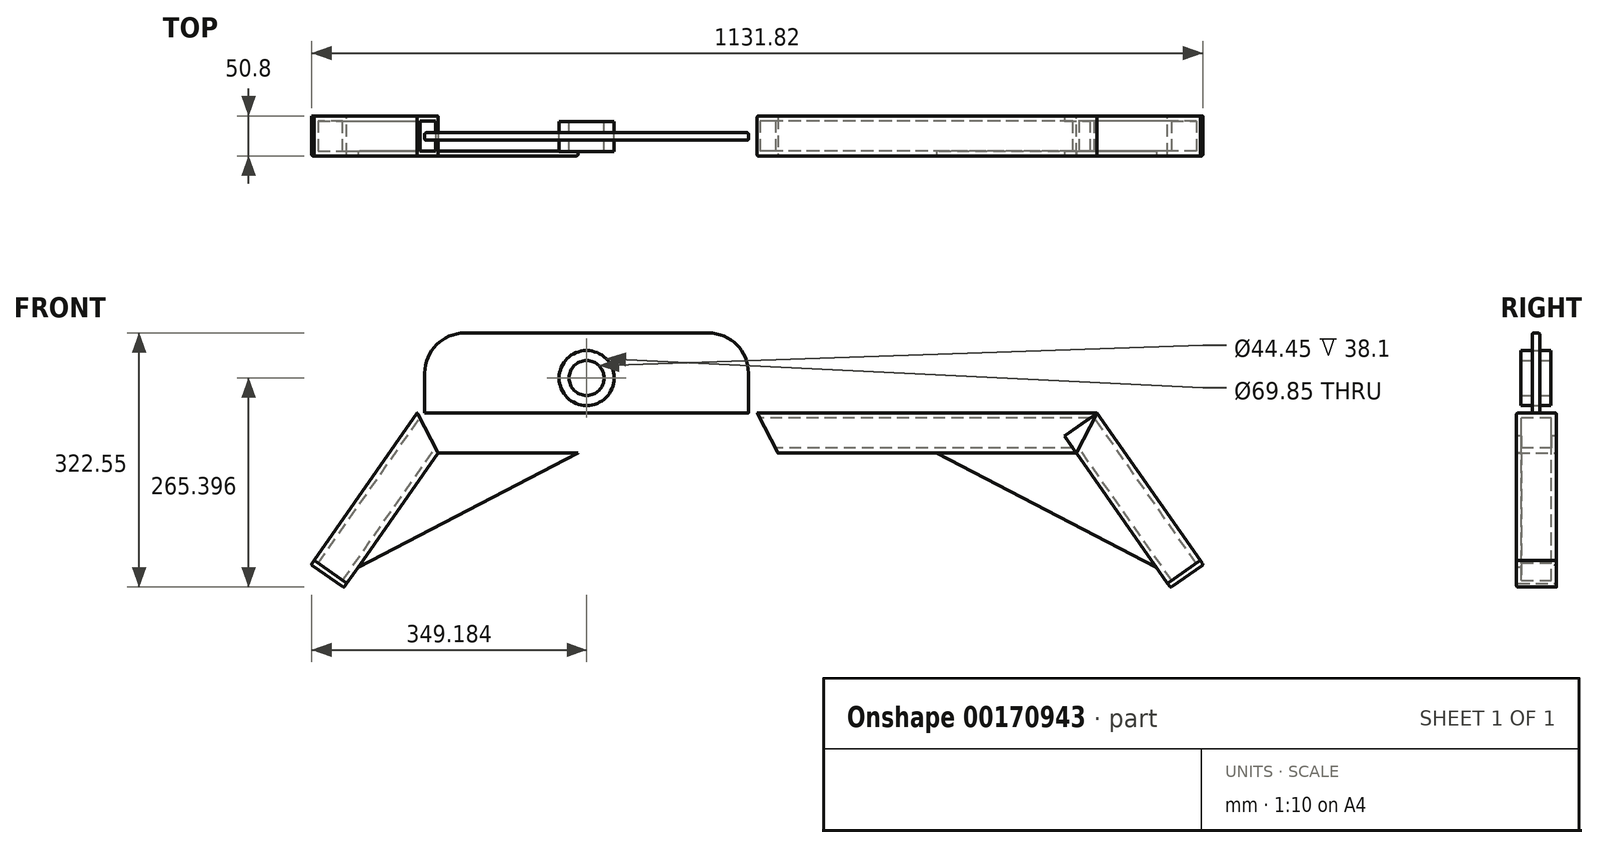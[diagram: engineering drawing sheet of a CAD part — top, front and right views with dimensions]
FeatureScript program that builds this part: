
annotation { "Feature Type Name" : "Feature", "Feature Type Description" : "" }
export const myFeature = defineFeature(function(context is Context, id is Id, definition is map)
    precondition{}
    {
        {
            var Q0;
            Q0=qCreatedBy(makeId("Right.planeOp"),FACE);
            var sketch = newSketch(context, id + "F0", { "sketchPlane" : qUnion([Q0])});
            skLineSegment(sketch, "E0.bottom", {"start": v(-57.95, 45.94) * mm, "end": v(-7.15, 45.94) * mm});
            skLineSegment(sketch, "E0.top", {"start": v(-57.95, -4.86) * mm, "end": v(-7.15, -4.86) * mm});
            skLineSegment(sketch, "E0.left", {"start": v(-57.95, 45.94) * mm, "end": v(-57.95, -4.86) * mm});
            skLineSegment(sketch, "E0.right", {"start": v(-7.15, 45.94) * mm, "end": v(-7.15, -4.86) * mm});
            skLineSegment(sketch, "E1.0", {"start": v(-13.5, 39.59) * mm, "end": v(-13.5, 1.49) * mm});
            skLineSegment(sketch, "E1.1", {"start": v(-51.6, 39.59) * mm, "end": v(-13.5, 39.59) * mm});
            skLineSegment(sketch, "E1.2", {"start": v(-51.6, 39.59) * mm, "end": v(-51.6, 1.49) * mm});
            skLineSegment(sketch, "E1.3", {"start": v(-51.6, 1.49) * mm, "end": v(-13.5, 1.49) * mm});
            skSolve(sketch);
        }
        {
            var Q0;
            Q0=makeQuery(id+"F0.imprint","IMPRINT",FACE,{"disambiguationData":[TD([[makeQuery(id+"F0.imprint","IMPRINT",EDGE,{"derivedFrom":sQuery(id+"F0.wireOp",EDGE,"E0.bottom")}),-1.0]])]});
            extrude(context, id + "F1", {"entities" : qUnion([Q0]), "depth" : 431.8 * mm});
        }
        {
            var Q0;
            Q0=makeQuery(id+"F1.opExtrude","SWEPT_FACE",FACE,{"disambiguationData":[OSD([sQuery(id+"F0.wireOp",EDGE,"E0.right")])]});
            var sketch = newSketch(context, id + "F2", { "sketchPlane" : qUnion([Q0])});
            skLineSegment(sketch, "E2", {"start": v(-431.8, 45.94) * mm, "end": v(-405.36, -4.86) * mm});
            skSolve(sketch);
        }
        {
            var Q0;
            {var subQ0=sQuery(id+"F2.wireOp",EDGE,"E2");Q0=makeQuery(id+"F2.imprint","IMPRINT",FACE,{"disambiguationData":[TD([[makeQuery(id+"F2.imprint","IMPRINT",EDGE,{"derivedFrom":subQ0}),-1.0]])]});}
            extrude(context, id + "F3", {"entities" : qUnion([Q0]), "operationType" : NewBodyOperationType.REMOVE, "endBound" : BoundingType.THROUGH_ALL, "oppositeDirection" : true, "depth" : 25.4 * mm});
        }
        {
            var Q0;
            Q0=makeQuery(id+"F1.opExtrude","SWEPT_FACE",FACE,{"disambiguationData":[OSD([sQuery(id+"F0.wireOp",EDGE,"E0.right")])]});
            var sketch = newSketch(context, id + "F4", { "sketchPlane" : qUnion([Q0])});
            skLineSegment(sketch, "E3", {"start": v(-431.8, 45.94) * mm, "end": v(-431.8, -57.78) * mm});
            skLineSegment(sketch, "E4", {"start": v(-431.8, 45.94) * mm, "end": v(-336.9, -20.51) * mm});
            skSolve(sketch);
        }
        {
            var Q0;
            Q0=qCreatedBy(makeId("Right.planeOp"),FACE);
            var Q1;
            Q1=sQuery(id+"F4.wireOp",EDGE,"E4");
            cPlane(context, id + "F5", {"entities" : qUnion([Q0, Q1]), "cplaneType" : CPlaneType.LINE_ANGLE, "offset" : 25.4 * mm, "angle" : 0 * degree, "width" : 152.4 * mm, "height" : 152.4 * mm});
        }
        {
            var Q0;
            Q0=qCreatedBy(id+"F5.planeOp",FACE);
            var sketch = newSketch(context, id + "F6", { "sketchPlane" : qUnion([Q0])});
            skLineSegment(sketch, "E5", {"start": v(380.06, -7.15) * mm, "end": v(380.06, -57.95) * mm});
            skLineSegment(sketch, "E6", {"start": v(380.06, -57.95) * mm, "end": v(329.26, -57.95) * mm});
            skLineSegment(sketch, "E7", {"start": v(329.26, -57.95) * mm, "end": v(329.26, -7.15) * mm});
            skLineSegment(sketch, "E8", {"start": v(329.26, -7.15) * mm, "end": v(380.06, -7.15) * mm});
            skLineSegment(sketch, "E9.0", {"start": v(373.7, -13.5) * mm, "end": v(373.7, -51.6) * mm});
            skLineSegment(sketch, "E9.1", {"start": v(335.6, -13.5) * mm, "end": v(373.7, -13.5) * mm});
            skLineSegment(sketch, "E9.2", {"start": v(335.6, -51.6) * mm, "end": v(335.6, -13.5) * mm});
            skLineSegment(sketch, "E9.3", {"start": v(373.7, -51.6) * mm, "end": v(335.6, -51.6) * mm});
            skSolve(sketch);
        }
        {
            var Q0;
            Q0=makeQuery(id+"F6.imprint","IMPRINT",FACE,{"disambiguationData":[TD([[makeQuery(id+"F6.imprint","IMPRINT",EDGE,{"derivedFrom":sQuery(id+"F6.wireOp",EDGE,"E5")}),-1.0]])]});
            extrude(context, id + "F7", {"entities" : qUnion([Q0]), "oppositeDirection" : true, "depth" : 228.6 * mm});
        }
        {
            var Q0;
            Q0=makeQuery(id+"F7.opExtrude","SWEPT_FACE",FACE,{"disambiguationData":[OSD([sQuery(id+"F6.wireOp",EDGE,"E6")])]});
            var sketch = newSketch(context, id + "F8", { "sketchPlane" : qUnion([Q0])});
            skLineSegment(sketch, "E10", {"start": v(431.8, 45.94) * mm, "end": v(397.13, -20.67) * mm});
            skSolve(sketch);
        }
        {
            var Q0;
            {var subQ1=sQuery(id+"F6.wireOp",EDGE,"E6");var subQ2=makeQuery(id+"F7.opExtrude","CAP_EDGE",EDGE,{"disambiguationData":[OSD([subQ1])],"isStart":true});Q0=makeQuery(id+"F8.imprint","IMPRINT",FACE,{"disambiguationData":[TD([[makeQuery(id+"F8.imprint","IMPRINT",EDGE,{"derivedFrom":subQ2}),1.0]])]});}
            extrude(context, id + "F9", {"entities" : qUnion([Q0]), "operationType" : NewBodyOperationType.REMOVE, "endBound" : BoundingType.THROUGH_ALL, "oppositeDirection" : true, "depth" : 25.4 * mm});
        }
        {
            var Q0;
            Q0=makeQuery(id+"F1.opExtrude","SWEPT_FACE",FACE,{"disambiguationData":[OSD([sQuery(id+"F0.wireOp",EDGE,"E0.left")])]});
            var sketch = newSketch(context, id + "F10", { "sketchPlane" : qUnion([Q0])});
            skLineSegment(sketch, "E11", {"start": v(227.56, -4.86) * mm, "end": v(405.36, -4.86) * mm});
            skLineSegment(sketch, "E12", {"start": v(405.36, -4.86) * mm, "end": v(507.34, -150.5) * mm});
            skLineSegment(sketch, "E13", {"start": v(227.56, -4.86) * mm, "end": v(507.34, -150.5) * mm});
            skSolve(sketch);
        }
        {
            var Q0;
            Q0=makeQuery(id+"F10.imprint","IMPRINT",FACE,{"disambiguationData":[TD([[makeQuery(id+"F10.imprint","IMPRINT",EDGE,{"derivedFrom":sQuery(id+"F10.wireOp",EDGE,"E11")}),1.0]])]});
            extrude(context, id + "F11", {"entities" : qUnion([Q0]), "oppositeDirection" : true, "depth" : 6.35 * mm});
        }
        {
            var Q0;
            Q0=makeQuery(id+"F7.opExtrude","CAP_FACE",FACE,{"disambiguationData":[OSD([sQuery(id+"F6.wireOp",EDGE,"E5"),sQuery(id+"F6.wireOp",EDGE,"E6"),sQuery(id+"F6.wireOp",EDGE,"E7"),sQuery(id+"F6.wireOp",EDGE,"E8"),sQuery(id+"F6.wireOp",EDGE,"E9.0"),sQuery(id+"F6.wireOp",EDGE,"E9.1"),sQuery(id+"F6.wireOp",EDGE,"E9.2"),sQuery(id+"F6.wireOp",EDGE,"E9.3")])],"isStart":false});
            var sketch = newSketch(context, id + "F12", { "sketchPlane" : qUnion([Q0])});
            skLineSegment(sketch, "E14.bottom", {"start": v(329.26, 57.95) * mm, "end": v(380.06, 57.95) * mm});
            skLineSegment(sketch, "E14.top", {"start": v(329.26, 7.15) * mm, "end": v(380.06, 7.15) * mm});
            skLineSegment(sketch, "E14.left", {"start": v(329.26, 57.95) * mm, "end": v(329.26, 7.15) * mm});
            skLineSegment(sketch, "E14.right", {"start": v(380.06, 57.95) * mm, "end": v(380.06, 7.15) * mm});
            skSolve(sketch);
        }
        {
            var Q0;
            Q0=makeQuery(id+"F12.imprint","IMPRINT",FACE,{"disambiguationData":[TD([[makeQuery(id+"F12.imprint","IMPRINT",EDGE,{"derivedFrom":makeQuery(id+"F7.opExtrude","CAP_EDGE",EDGE,{"disambiguationData":[OSD([sQuery(id+"F6.wireOp",EDGE,"E9.0")])],"isStart":false})}),1.0]])]});
            var Q1;
            Q1=makeQuery(id+"F12.imprint","IMPRINT",FACE,{"disambiguationData":[TD([[makeQuery(id+"F12.imprint","IMPRINT",EDGE,{"derivedFrom":sQuery(id+"F12.wireOp",EDGE,"E14.bottom")}),1.0]])]});
            extrude(context, id + "F13", {"entities" : qUnion([Q0, Q1]), "depth" : 6.35 * mm});
        }
        {
            var Q0;
            Q0=makeQuery(id+"F7.opExtrude","SWEPT_BODY",BODY,{"disambiguationData":[OSD([sQuery(id+"F6.wireOp",EDGE,"E5"),sQuery(id+"F6.wireOp",EDGE,"E6"),sQuery(id+"F6.wireOp",EDGE,"E7"),sQuery(id+"F6.wireOp",EDGE,"E8"),sQuery(id+"F6.wireOp",EDGE,"E9.0"),sQuery(id+"F6.wireOp",EDGE,"E9.1"),sQuery(id+"F6.wireOp",EDGE,"E9.2"),sQuery(id+"F6.wireOp",EDGE,"E9.3")])]});
            var Q1;
            Q1=makeQuery(id+"F1.opExtrude","SWEPT_BODY",BODY,{"disambiguationData":[OSD([sQuery(id+"F0.wireOp",EDGE,"E0.bottom"),sQuery(id+"F0.wireOp",EDGE,"E0.top"),sQuery(id+"F0.wireOp",EDGE,"E0.left"),sQuery(id+"F0.wireOp",EDGE,"E0.right"),sQuery(id+"F0.wireOp",EDGE,"E1.0"),sQuery(id+"F0.wireOp",EDGE,"E1.1"),sQuery(id+"F0.wireOp",EDGE,"E1.2"),sQuery(id+"F0.wireOp",EDGE,"E1.3")])]});
            var Q2;
            Q2=makeQuery(id+"F11.opExtrude","SWEPT_BODY",BODY,{"disambiguationData":[OSD([sQuery(id+"F10.wireOp",EDGE,"E11"),sQuery(id+"F10.wireOp",EDGE,"E12"),sQuery(id+"F10.wireOp",EDGE,"E13")])]});
            var Q3;
            Q3=makeQuery(id+"F13.opExtrude","SWEPT_BODY",BODY,{"disambiguationData":[OSD([sQuery(id+"F12.wireOp",EDGE,"E14.bottom"),sQuery(id+"F12.wireOp",EDGE,"E14.top"),sQuery(id+"F12.wireOp",EDGE,"E14.left"),sQuery(id+"F12.wireOp",EDGE,"E14.right")])]});
            var Q4;
            Q4=makeQuery(id+"F1.opExtrude","CAP_FACE",FACE,{"disambiguationData":[OSD([sQuery(id+"F0.wireOp",EDGE,"E0.bottom"),sQuery(id+"F0.wireOp",EDGE,"E0.top"),sQuery(id+"F0.wireOp",EDGE,"E0.left"),sQuery(id+"F0.wireOp",EDGE,"E0.right"),sQuery(id+"F0.wireOp",EDGE,"E1.0"),sQuery(id+"F0.wireOp",EDGE,"E1.1"),sQuery(id+"F0.wireOp",EDGE,"E1.2"),sQuery(id+"F0.wireOp",EDGE,"E1.3")])],"isStart":true});
            mirror(context, id + "F14", {"entities" : qUnion([Q0, Q1, Q2, Q3]), "mirrorPlane" : qUnion([Q4])});
        }
        {
            var Q0;
            Q0=makeQuery(id+"F14.opPattern","COPY",FACE,{"derivedFrom":makeQuery(id+"F1.opExtrude","SWEPT_FACE",FACE,{"disambiguationData":[OSD([sQuery(id+"F0.wireOp",EDGE,"E0.bottom")])]}),"instanceName":"1"});
            var sketch = newSketch(context, id + "F15", { "sketchPlane" : qUnion([Q0])});
            skLineSegment(sketch, "E15.bottom", {"start": v(-422.28, -28.5) * mm, "end": v(-11.18, -28.5) * mm});
            skLineSegment(sketch, "E15.top", {"start": v(-422.28, -38.03) * mm, "end": v(-11.18, -38.03) * mm});
            skLineSegment(sketch, "E15.left", {"start": v(-422.28, -28.5) * mm, "end": v(-422.28, -38.03) * mm});
            skLineSegment(sketch, "E15.right", {"start": v(-11.18, -28.5) * mm, "end": v(-11.18, -38.03) * mm});
            skSolve(sketch);
        }
        {
            var Q0;
            {var subQ0=sQuery(id+"F15.wireOp",EDGE,"E15.left");Q0=makeQuery(id+"F15.imprint","IMPRINT",FACE,{"disambiguationData":[TD([[makeQuery(id+"F15.imprint","IMPRINT",EDGE,{"derivedFrom":subQ0}),1.0]])]});}
            var Q1;
            {var subQ0=sQuery(id+"F15.wireOp",EDGE,"E15.right");Q1=makeQuery(id+"F15.imprint","IMPRINT",FACE,{"disambiguationData":[TD([[makeQuery(id+"F15.imprint","IMPRINT",EDGE,{"derivedFrom":subQ0}),-1.0]])]});}
            extrude(context, id + "F16", {"entities" : qUnion([Q0, Q1]), "depth" : 101.6 * mm});
        }
        {
            var Q0;
            Q0=makeQuery(id+"F16.opExtrude","CAP_EDGE",EDGE,{"disambiguationData":[OSD([sQuery(id+"F15.wireOp",EDGE,"E15.left")])],"isStart":false});
            var Q1;
            Q1=makeQuery(id+"F16.opExtrude","CAP_EDGE",EDGE,{"disambiguationData":[OSD([sQuery(id+"F15.wireOp",EDGE,"E15.right")])],"isStart":false});
            fillet(context, id + "F17", {"entities" : qUnion([Q0, Q1]), "radius" : 50.8 * mm, "tangentPropagation" : true, "allowEdgeOverflow" : false});
        }
        {
            var Q0;
            Q0=makeQuery(id+"F16.opExtrude","SWEPT_FACE",FACE,{"disambiguationData":[OSD([sQuery(id+"F15.wireOp",EDGE,"E15.top")])]});
            var sketch = newSketch(context, id + "F18", { "sketchPlane" : qUnion([Q0])});
            skCircle(sketch, "E16", {"center": v(-216.73, 90.39) * mm, "radius": 22.23 * mm});
            skPoint(sketch, "E16.centerSnap0", {"position": v(-216.73, 45.94) * mm});
            skSolve(sketch);
        }
        {
            var Q0;
            Q0=makeQuery(id+"F18.imprint","IMPRINT",FACE,{"disambiguationData":[TD([[makeQuery(id+"F18.imprint","IMPRINT",EDGE,{"derivedFrom":sQuery(id+"F18.wireOp",EDGE,"E16")}),1.0]])]});
            extrude(context, id + "F19", {"entities" : qUnion([Q0]), "operationType" : NewBodyOperationType.REMOVE, "oppositeDirection" : true, "depth" : 25.4 * mm});
        }
        {
            var Q0;
            Q0=makeQuery(id+"F16.opExtrude","SWEPT_FACE",FACE,{"disambiguationData":[OSD([sQuery(id+"F15.wireOp",EDGE,"E15.top")])]});
            var sketch = newSketch(context, id + "F20", { "sketchPlane" : qUnion([Q0])});
            skCircle(sketch, "E17", {"center": v(-216.73, 90.39) * mm, "radius": 34.93 * mm});
            skSolve(sketch);
        }
        {
            var Q0;
            Q0=makeQuery(id+"F20.imprint","IMPRINT",FACE,{"disambiguationData":[TD([[makeQuery(id+"F20.imprint","IMPRINT",EDGE,{"derivedFrom":sQuery(id+"F20.wireOp",EDGE,"E17")}),1.0]])]});
            extrude(context, id + "F21", {"entities" : qUnion([Q0]), "depth" : 14.29 * mm, "hasSecondDirection" : true, "secondDirectionOppositeDirection" : true, "secondDirectionDepth" : 23.8 * mm});
        }
        {
            var Q0;
            Q0=makeQuery(id+"F21.opExtrude","SWEPT_BODY",BODY,{"disambiguationData":[OSD([sQuery(id+"F18.wireOp",EDGE,"E16"),sQuery(id+"F20.wireOp",EDGE,"E17")])]});
            var Q1;
            Q1=makeQuery(id+"F16.opExtrude","SWEPT_BODY",BODY,{"disambiguationData":[OSD([sQuery(id+"F15.wireOp",EDGE,"E15.bottom"),sQuery(id+"F15.wireOp",EDGE,"E15.top"),sQuery(id+"F15.wireOp",EDGE,"E15.left"),sQuery(id+"F15.wireOp",EDGE,"E15.right")])]});
            booleanBodies(context, id + "F22", {"operationType" : BooleanOperationType.SUBTRACTION, "tools" : qUnion([Q0]), "targets" : qUnion([Q1]), "keepTools" : true});
        }
        {
            var Q0;
            Q0=makeQuery(id+"F1.opExtrude","SWEPT_FACE",FACE,{"disambiguationData":[OSD([sQuery(id+"F0.wireOp",EDGE,"E0.left")])]});
            var sketch = newSketch(context, id + "F23", { "sketchPlane" : qUnion([Q0])});
            skLineSegment(sketch, "E18", {"start": v(0, 45.94) * mm, "end": v(26.44, -4.86) * mm});
            skSolve(sketch);
        }
        {
            var Q0;
            {var subQ0=sQuery(id+"F23.wireOp",EDGE,"E18");Q0=makeQuery(id+"F23.imprint","IMPRINT",FACE,{"disambiguationData":[TD([[makeQuery(id+"F23.imprint","IMPRINT",EDGE,{"derivedFrom":subQ0}),-1.0]])]});}
            extrude(context, id + "F24", {"entities" : qUnion([Q0]), "operationType" : NewBodyOperationType.REMOVE, "endBound" : BoundingType.THROUGH_ALL, "oppositeDirection" : true, "depth" : 25.4 * mm});
        }
        {
            var Q0;
            Q0=makeQuery(id+"F14.opPattern","COPY",BODY,{"derivedFrom":makeQuery(id+"F1.opExtrude","SWEPT_BODY",BODY,{"disambiguationData":[OSD([sQuery(id+"F0.wireOp",EDGE,"E0.bottom"),sQuery(id+"F0.wireOp",EDGE,"E0.top"),sQuery(id+"F0.wireOp",EDGE,"E0.left"),sQuery(id+"F0.wireOp",EDGE,"E0.right"),sQuery(id+"F0.wireOp",EDGE,"E1.0"),sQuery(id+"F0.wireOp",EDGE,"E1.1"),sQuery(id+"F0.wireOp",EDGE,"E1.2"),sQuery(id+"F0.wireOp",EDGE,"E1.3")])]}),"instanceName":"1"});
            deleteBodies(context, id + "F25", {"entities" : qUnion([Q0])});
        }
        {
            var Q0;
            Q0=makeQuery(id+"F14.opPattern","COPY",EDGE,{"derivedFrom":makeQuery(id+"F11.opExtrude","CAP_EDGE",EDGE,{"disambiguationData":[OSD([sQuery(id+"F10.wireOp",EDGE,"E13")])],"isStart":true}),"instanceName":"1"});
            var Q1;
            Q1=makeQuery(id+"F14.opPattern","COPY",EDGE,{"derivedFrom":makeQuery(id+"F11.opExtrude","CAP_EDGE",EDGE,{"disambiguationData":[OSD([sQuery(id+"F10.wireOp",EDGE,"E13")])],"isStart":false}),"instanceName":"1"});
            var Q2;
            Q2=makeQuery(id+"F14.opPattern","COPY",EDGE,{"derivedFrom":makeQuery(id+"F7.opExtrude","SWEPT_EDGE",EDGE,{"disambiguationData":[OSD([sQuery(id+"F6.wireOp",EDGE,"E7"),sQuery(id+"F6.wireOp",EDGE,"E8")])]}),"instanceName":"1"});
            var Q3;
            Q3=makeQuery(id+"F14.opPattern","COPY",EDGE,{"derivedFrom":makeQuery(id+"F7.opExtrude","SWEPT_EDGE",EDGE,{"disambiguationData":[OSD([sQuery(id+"F6.wireOp",EDGE,"E6"),sQuery(id+"F6.wireOp",EDGE,"E7")])]}),"instanceName":"1"});
            var Q4;
            Q4=makeQuery(id+"F14.opPattern","COPY",EDGE,{"derivedFrom":makeQuery(id+"F13.opExtrude","CAP_EDGE",EDGE,{"disambiguationData":[OSD([sQuery(id+"F12.wireOp",EDGE,"E14.left")])],"isStart":false}),"instanceName":"1"});
            var Q5;
            Q5=makeQuery(id+"F14.opPattern","COPY",EDGE,{"derivedFrom":makeQuery(id+"F13.opExtrude","SWEPT_EDGE",EDGE,{"disambiguationData":[OSD([sQuery(id+"F12.wireOp",EDGE,"E14.bottom"),sQuery(id+"F12.wireOp",EDGE,"E14.left")])]}),"instanceName":"1"});
            var Q6;
            Q6=makeQuery(id+"F14.opPattern","COPY",EDGE,{"derivedFrom":makeQuery(id+"F13.opExtrude","CAP_EDGE",EDGE,{"disambiguationData":[OSD([sQuery(id+"F12.wireOp",EDGE,"E14.bottom")])],"isStart":false}),"instanceName":"1"});
            var Q7;
            Q7=makeQuery(id+"F14.opPattern","COPY",EDGE,{"derivedFrom":makeQuery(id+"F13.opExtrude","SWEPT_EDGE",EDGE,{"disambiguationData":[OSD([sQuery(id+"F12.wireOp",EDGE,"E14.top"),sQuery(id+"F12.wireOp",EDGE,"E14.left")])]}),"instanceName":"1"});
            var Q8;
            Q8=makeQuery(id+"F14.opPattern","COPY",EDGE,{"derivedFrom":makeQuery(id+"F13.opExtrude","CAP_EDGE",EDGE,{"disambiguationData":[OSD([sQuery(id+"F12.wireOp",EDGE,"E14.right")])],"isStart":false}),"instanceName":"1"});
            var Q9;
            Q9=makeQuery(id+"F14.opPattern","COPY",EDGE,{"derivedFrom":makeQuery(id+"F7.opExtrude","SWEPT_EDGE",EDGE,{"disambiguationData":[OSD([sQuery(id+"F6.wireOp",EDGE,"E5"),sQuery(id+"F6.wireOp",EDGE,"E6")])]}),"instanceName":"1"});
            var Q10;
            Q10=makeQuery(id+"F14.opPattern","COPY",EDGE,{"derivedFrom":makeQuery(id+"F13.opExtrude","SWEPT_EDGE",EDGE,{"disambiguationData":[OSD([sQuery(id+"F12.wireOp",EDGE,"E14.bottom"),sQuery(id+"F12.wireOp",EDGE,"E14.right")])]}),"instanceName":"1"});
            var Q11;
            Q11=makeQuery(id+"F14.opPattern","COPY",EDGE,{"derivedFrom":makeQuery(id+"F7.opExtrude","SWEPT_EDGE",EDGE,{"disambiguationData":[OSD([sQuery(id+"F6.wireOp",EDGE,"E5"),sQuery(id+"F6.wireOp",EDGE,"E8")])]}),"instanceName":"1"});
            var Q12;
            Q12=makeQuery(id+"F16.opExtrude","SWEPT_EDGE",EDGE,{"disambiguationData":[OSD([sQuery(id+"F15.wireOp",EDGE,"E15.bottom"),sQuery(id+"F15.wireOp",EDGE,"E15.left")])]});
            var Q13;
            Q13=makeQuery(id+"F16.opExtrude","SWEPT_EDGE",EDGE,{"disambiguationData":[OSD([sQuery(id+"F15.wireOp",EDGE,"E15.top"),sQuery(id+"F15.wireOp",EDGE,"E15.left")])]});
            var Q14;
            Q14=makeQuery(id+"F17.opFillet","BLEND_EDGE",EDGE,{"blendedFrom":[makeQuery(id+"F16.opExtrude","CAP_EDGE",EDGE,{"disambiguationData":[OSD([sQuery(id+"F15.wireOp",EDGE,"E15.left")])],"isStart":false}),makeQuery(id+"F16.opExtrude","SWEPT_FACE",FACE,{"disambiguationData":[OSD([sQuery(id+"F15.wireOp",EDGE,"E15.bottom")])]})],"blendedInto":[makeQuery(id+"F16.opExtrude","SWEPT_FACE",FACE,{"disambiguationData":[OSD([sQuery(id+"F15.wireOp",EDGE,"E15.bottom")])]})]});
            var Q15;
            Q15=makeQuery(id+"F17.opFillet","BLEND_EDGE",EDGE,{"blendedFrom":[makeQuery(id+"F16.opExtrude","CAP_EDGE",EDGE,{"disambiguationData":[OSD([sQuery(id+"F15.wireOp",EDGE,"E15.left")])],"isStart":false}),makeQuery(id+"F16.opExtrude","SWEPT_FACE",FACE,{"disambiguationData":[OSD([sQuery(id+"F15.wireOp",EDGE,"E15.top")])]})],"blendedInto":[makeQuery(id+"F16.opExtrude","SWEPT_FACE",FACE,{"disambiguationData":[OSD([sQuery(id+"F15.wireOp",EDGE,"E15.top")])]})]});
            var Q16;
            Q16=makeQuery(id+"F1.opExtrude","SWEPT_EDGE",EDGE,{"disambiguationData":[OSD([sQuery(id+"F0.wireOp",EDGE,"E0.top"),sQuery(id+"F0.wireOp",EDGE,"E0.right")])]});
            var Q17;
            Q17=makeQuery(id+"F1.opExtrude","SWEPT_EDGE",EDGE,{"disambiguationData":[OSD([sQuery(id+"F0.wireOp",EDGE,"E0.bottom"),sQuery(id+"F0.wireOp",EDGE,"E0.right")])]});
            var Q18;
            Q18=makeQuery(id+"F1.opExtrude","SWEPT_EDGE",EDGE,{"disambiguationData":[OSD([sQuery(id+"F0.wireOp",EDGE,"E0.bottom"),sQuery(id+"F0.wireOp",EDGE,"E0.left")])]});
            var Q19;
            Q19=makeQuery(id+"F1.opExtrude","SWEPT_EDGE",EDGE,{"disambiguationData":[OSD([sQuery(id+"F0.wireOp",EDGE,"E0.top"),sQuery(id+"F0.wireOp",EDGE,"E0.left")])]});
            var Q20;
            Q20=makeQuery(id+"F11.opExtrude","CAP_EDGE",EDGE,{"disambiguationData":[OSD([sQuery(id+"F10.wireOp",EDGE,"E13")])],"isStart":true});
            var Q21;
            Q21=makeQuery(id+"F11.opExtrude","CAP_EDGE",EDGE,{"disambiguationData":[OSD([sQuery(id+"F10.wireOp",EDGE,"E13")])],"isStart":false});
            var Q22;
            Q22=makeQuery(id+"F7.opExtrude","SWEPT_EDGE",EDGE,{"disambiguationData":[OSD([sQuery(id+"F6.wireOp",EDGE,"E6"),sQuery(id+"F6.wireOp",EDGE,"E7")])]});
            var Q23;
            Q23=makeQuery(id+"F7.opExtrude","SWEPT_EDGE",EDGE,{"disambiguationData":[OSD([sQuery(id+"F6.wireOp",EDGE,"E5"),sQuery(id+"F6.wireOp",EDGE,"E6")])]});
            var Q24;
            Q24=makeQuery(id+"F7.opExtrude","SWEPT_EDGE",EDGE,{"disambiguationData":[OSD([sQuery(id+"F6.wireOp",EDGE,"E7"),sQuery(id+"F6.wireOp",EDGE,"E8")])]});
            var Q25;
            Q25=makeQuery(id+"F13.opExtrude","SWEPT_EDGE",EDGE,{"disambiguationData":[OSD([sQuery(id+"F12.wireOp",EDGE,"E14.bottom"),sQuery(id+"F12.wireOp",EDGE,"E14.left")])]});
            var Q26;
            Q26=makeQuery(id+"F13.opExtrude","SWEPT_EDGE",EDGE,{"disambiguationData":[OSD([sQuery(id+"F12.wireOp",EDGE,"E14.top"),sQuery(id+"F12.wireOp",EDGE,"E14.left")])]});
            var Q27;
            Q27=makeQuery(id+"F13.opExtrude","SWEPT_EDGE",EDGE,{"disambiguationData":[OSD([sQuery(id+"F12.wireOp",EDGE,"E14.bottom"),sQuery(id+"F12.wireOp",EDGE,"E14.right")])]});
            var Q28;
            Q28=makeQuery(id+"F13.opExtrude","CAP_EDGE",EDGE,{"disambiguationData":[OSD([sQuery(id+"F12.wireOp",EDGE,"E14.bottom")])],"isStart":false});
            var Q29;
            Q29=makeQuery(id+"F13.opExtrude","CAP_EDGE",EDGE,{"disambiguationData":[OSD([sQuery(id+"F12.wireOp",EDGE,"E14.left")])],"isStart":false});
            var Q30;
            Q30=makeQuery(id+"F13.opExtrude","CAP_EDGE",EDGE,{"disambiguationData":[OSD([sQuery(id+"F12.wireOp",EDGE,"E14.top")])],"isStart":false});
            var Q31;
            Q31=makeQuery(id+"F13.opExtrude","CAP_EDGE",EDGE,{"disambiguationData":[OSD([sQuery(id+"F12.wireOp",EDGE,"E14.right")])],"isStart":false});
            var Q32;
            Q32=makeQuery(id+"F7.opExtrude","SWEPT_EDGE",EDGE,{"disambiguationData":[OSD([sQuery(id+"F6.wireOp",EDGE,"E5"),sQuery(id+"F6.wireOp",EDGE,"E8")])]});
            fillet(context, id + "F26", {"entities" : qUnion([Q0, Q1, Q2, Q3, Q4, Q5, Q6, Q7, Q8, Q9, Q10, Q11, Q12, Q13, Q14, Q15, Q16, Q17, Q18, Q19, Q20, Q21, Q22, Q23, Q24, Q25, Q26, Q27, Q28, Q29, Q30, Q31, Q32]), "radius" : 1.65 * mm, "tangentPropagation" : true, "allowEdgeOverflow" : false});
        }
    });
